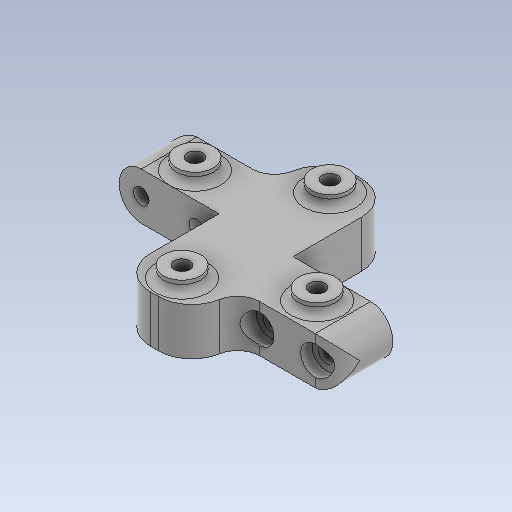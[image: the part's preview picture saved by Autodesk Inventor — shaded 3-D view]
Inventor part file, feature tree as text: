
AUTODESK INVENTOR PART (.ipt)
format: ipt  version: 2021 (Build 250183000, 183)  size: 346,624 bytes
history: native  units: mm
features: projected_geometry x13, extrude x6, sketch x6, pattern_circular x2, fillet x2, other x1
ambient origin geometry x8: Origin, YZ Plane, XZ Plane, XY Plane, X Axis, Y Axis, Z Axis, Center Point
bodies: Body1 (feature_tree)
feature tree (30):
  other  "솔리드1"
  extrude  "돌출1"  Depth=12.7mm TaperAngle=0.0deg
  extrude  "돌출6"  Depth=12.7mm
  extrude  "돌출7"  Depth=80.0mm
  pattern_circular  "원형 패턴3"  Count=2  [1 undecoded]
  extrude  "돌출8"  Depth=27.0mm
  fillet  "모깎기4"  Radius=15.0mm
  extrude  "돌출9"  Depth=55.0mm
  extrude  "돌출11"  Depth=4.2mm
  pattern_circular  "원형 패턴4"  [2 undecoded]
  fillet  "모깎기8"  Radius=15.0mm
  sketch  "스케치1"
  sketch  "스케치5"
  projected_geometry  "투영된 루프11"
  sketch  "스케치6"
  projected_geometry  "투영된 루프12"
  sketch  "스케치7"
  projected_geometry  "투영된 루프13"
  projected_geometry  "투영된 루프14"
  projected_geometry  "투영된 루프15"
  projected_geometry  "투영된 루프16"
  projected_geometry  "투영된 루프17"
  projected_geometry  "투영된 루프18"
  projected_geometry  "투영된 루프19"
  projected_geometry  "투영된 루프20"
  projected_geometry  "투영된 루프21"
  sketch  "스케치8"
  projected_geometry  "투영된 루프22"
  sketch  "스케치10"
  projected_geometry  "투영된 루프24"
note: 3 required parameter values undecoded (feature->parameter linkage not recoverable at this tier; creation-order binding heuristic only, values carry confidence <= 0.55)
